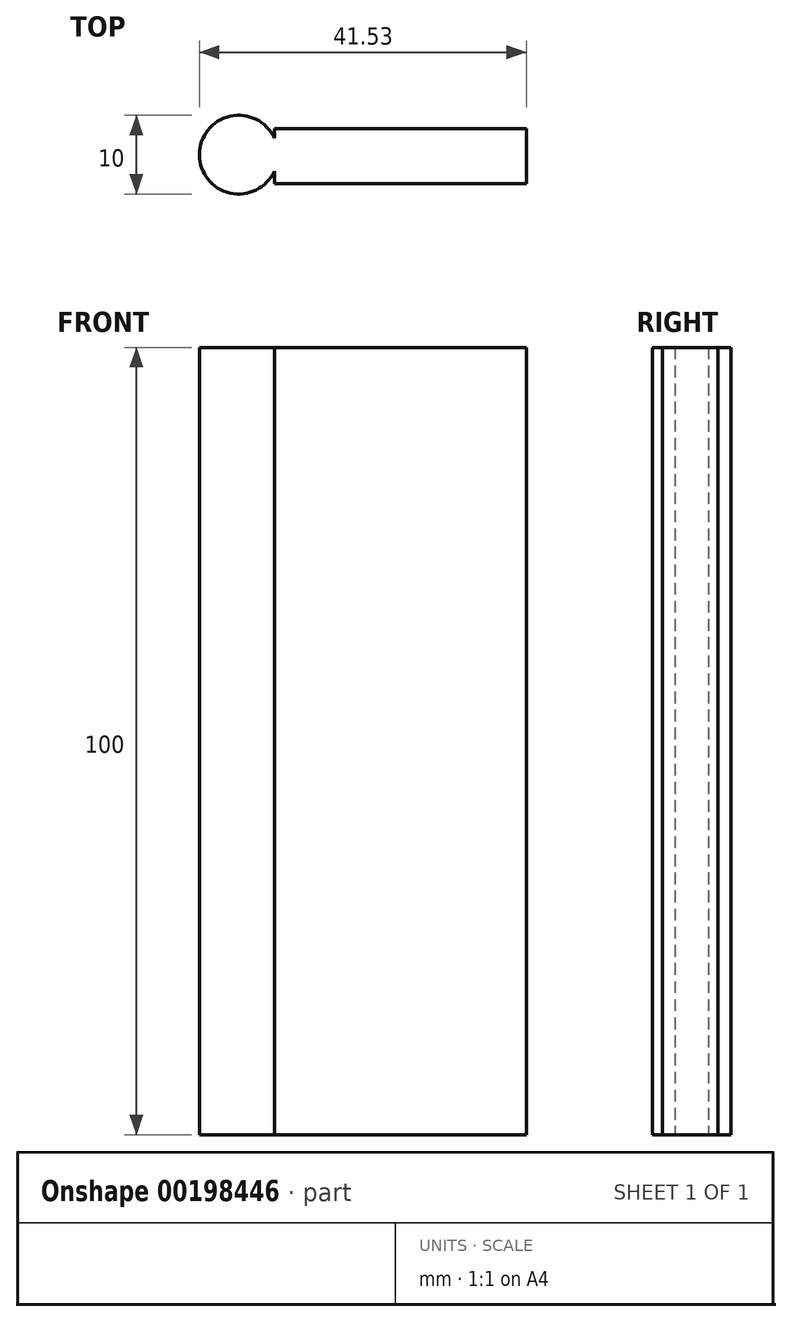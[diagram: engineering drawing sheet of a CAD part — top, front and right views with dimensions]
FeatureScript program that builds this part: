
annotation { "Feature Type Name" : "Feature", "Feature Type Description" : "" }
export const myFeature = defineFeature(function(context is Context, id is Id, definition is map)
    precondition{}
    {
        {
            var Q0;
            Q0=qCreatedBy(makeId("Top.planeOp"),FACE);
            var sketch = newSketch(context, id + "F0", { "sketchPlane" : qUnion([Q0])});
            skLineSegment(sketch, "E0.bottom", {"start": v(0, 0) * mm, "end": v(32, 0) * mm});
            skLineSegment(sketch, "E0.top", {"start": v(0, 7) * mm, "end": v(32, 7) * mm});
            skLineSegment(sketch, "E0.left", {"start": v(0, 0) * mm, "end": v(0, 1.57) * mm});
            skLineSegment(sketch, "E0.right", {"start": v(32, 0) * mm, "end": v(32, 7) * mm});
            skArc(sketch, "E1", {"start": v(0, 5.8) * mm, "mid": v(-9.53, 3.68) * mm, "end": v(0, 1.57) * mm});
            skLineSegment(sketch, "E2.trimOffspring", {"start": v(0, 5.8) * mm, "end": v(0, 7) * mm});
            skSolve(sketch);
        }
        {
            var Q0;
            {var subQ0=sQuery(id+"F0.wireOp",EDGE,"E1");var subQ1=sQuery(id+"F0.wireOp",EDGE,"E0.left");var subQ2=makeQuery(id+"F0.imprint","INTERSECT",VERTEX,{"disambiguationData":[OD(0.0)],"derivedFrom":[subQ1,subQ0]});Q0=makeQuery(id+"F0.imprint","IMPRINT",FACE,{"disambiguationData":[TD([[makeQuery(id+"F0.imprint","IMPRINT",EDGE,{"disambiguationData":[TD([[subQ2,-1.0]])],"derivedFrom":subQ1}),1.0]])]});}
            var Q1;
            {var subQ4=sQuery(id+"F0.wireOp",EDGE,"E0.bottom");Q1=makeQuery(id+"F0.imprint","IMPRINT",FACE,{"disambiguationData":[TD([[makeQuery(id+"F0.imprint","IMPRINT",EDGE,{"derivedFrom":subQ4}),1.0]])]});}
            extrude(context, id + "F1", {"entities" : qUnion([Q0, Q1]), "depth" : 100 * mm});
        }
    });
